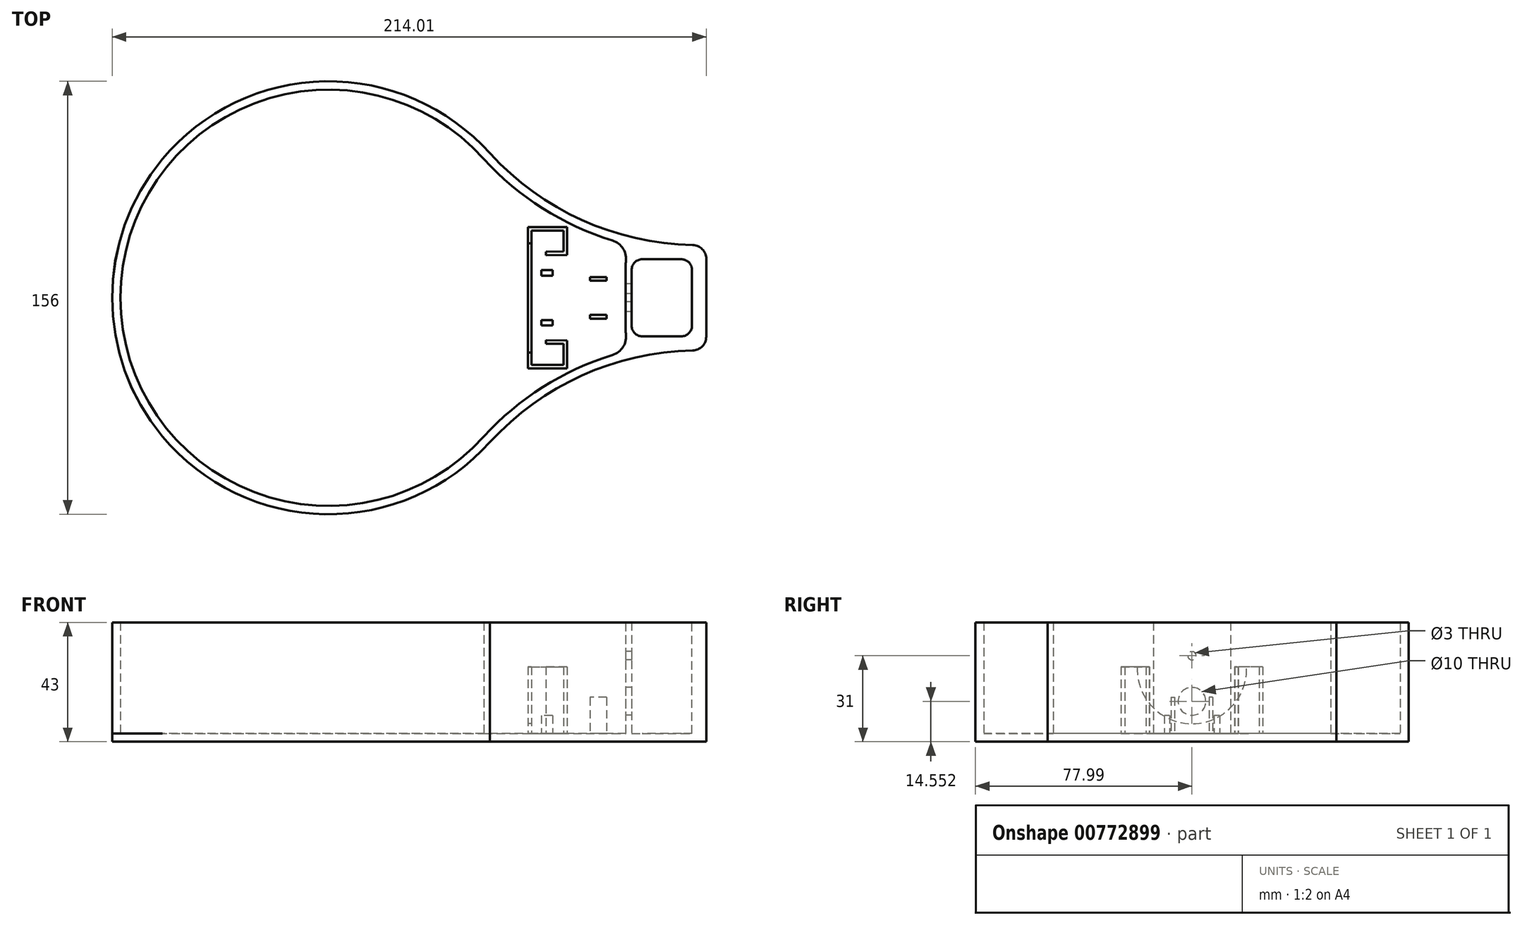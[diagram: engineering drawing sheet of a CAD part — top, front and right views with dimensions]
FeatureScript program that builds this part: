
annotation { "Feature Type Name" : "Feature", "Feature Type Description" : "" }
export const myFeature = defineFeature(function(context is Context, id is Id, definition is map)
    precondition{}
    {
        {
            var Q0;
            Q0=qCreatedBy(makeId("Top.planeOp"),FACE);
            var sketch = newSketch(context, id + "F0", { "sketchPlane" : qUnion([Q0])});
            skLineSegment(sketch, "E0", {"start": v(133, 0) * mm, "end": v(133, 16) * mm});
            skLineSegment(sketch, "E1", {"start": v(133, 16) * mm, "end": v(132.98, -16) * mm});
            skLineSegment(sketch, "E2", {"start": v(132.98, -16) * mm, "end": v(106.98, -16) * mm});
            skLineSegment(sketch, "E3", {"start": v(106.98, -16) * mm, "end": v(106.98, 16) * mm});
            skLineSegment(sketch, "E4", {"start": v(106.98, 16) * mm, "end": v(133, 16) * mm});
            skArc(sketch, "E5", {"start": v(55.9, 50) * mm, "mid": v(90.87, 24.88) * mm, "end": v(133, 16) * mm});
            skArc(sketch, "E6", {"start": v(132.98, -16) * mm, "mid": v(90.85, -24.88) * mm, "end": v(55.88, -50) * mm});
            skLineSegment(sketch, "E7", {"start": v(85.88, 25.5) * mm, "end": v(71.8, 25.5) * mm});
            skLineSegment(sketch, "E8", {"start": v(71.8, 25.5) * mm, "end": v(71.8, -25.5) * mm});
            skLineSegment(sketch, "E9", {"start": v(71.8, -25.5) * mm, "end": v(85.88, -25.5) * mm});
            skArc(sketch, "E10", {"start": v(55.9, 50) * mm, "mid": v(-75.01, 0.02) * mm, "end": v(55.88, -50) * mm});
            skLineSegment(sketch, "E11.0", {"start": v(109.1, 13.88) * mm, "end": v(130.88, 13.88) * mm});
            skLineSegment(sketch, "E11.1", {"start": v(109.1, -13.88) * mm, "end": v(109.1, 13.88) * mm});
            skLineSegment(sketch, "E11.2", {"start": v(130.86, -13.88) * mm, "end": v(109.1, -13.88) * mm});
            skLineSegment(sketch, "E11.3", {"start": v(130.88, 13.88) * mm, "end": v(130.86, -13.88) * mm});
            skLineSegment(sketch, "E12.0", {"start": v(84.6, 24.2) * mm, "end": v(73.1, 24.2) * mm});
            skLineSegment(sketch, "E12.2", {"start": v(73.1, -24.2) * mm, "end": v(84.6, -24.2) * mm});
            skLineSegment(sketch, "E12.3", {"start": v(73.1, 24.2) * mm, "end": v(73.1, -24.2) * mm});
            skLineSegment(sketch, "E13", {"start": v(85.88, 25.5) * mm, "end": v(85.88, 15.4) * mm});
            skLineSegment(sketch, "E14", {"start": v(85.88, 15.4) * mm, "end": v(78.28, 15.3) * mm});
            skLineSegment(sketch, "E15", {"start": v(78.28, 15.3) * mm, "end": v(78.27, 16.6) * mm});
            skLineSegment(sketch, "E16", {"start": v(78.27, 16.6) * mm, "end": v(84.6, 16.68) * mm});
            skLineSegment(sketch, "E17", {"start": v(85.88, -25.5) * mm, "end": v(85.88, -15.4) * mm});
            skLineSegment(sketch, "E18", {"start": v(85.88, -15.4) * mm, "end": v(78.28, -15.3) * mm});
            skLineSegment(sketch, "E19", {"start": v(78.28, -15.3) * mm, "end": v(78.28, -16.6) * mm});
            skLineSegment(sketch, "E20", {"start": v(78.28, -16.6) * mm, "end": v(84.6, -16.6) * mm});
            skLineSegment(sketch, "E21", {"start": v(84.6, -16.6) * mm, "end": v(84.6, -24.2) * mm});
            skLineSegment(sketch, "E22", {"start": v(84.6, 24.2) * mm, "end": v(84.6, 16.68) * mm});
            skArc(sketch, "E23.0", {"start": v(58.13, 52.01) * mm, "mid": v(93.46, 27.02) * mm, "end": v(136, 19.04) * mm});
            skArc(sketch, "E23.1", {"start": v(58.13, 52.01) * mm, "mid": v(-78.01, 0.02) * mm, "end": v(58.1, -52.01) * mm});
            skArc(sketch, "E23.2", {"start": v(135.98, -19.04) * mm, "mid": v(93.44, -27.02) * mm, "end": v(58.1, -52.01) * mm});
            skLineSegment(sketch, "E23.3", {"start": v(136, 19.04) * mm, "end": v(135.98, -19.04) * mm});
            skArc(sketch, "E24", {"start": v(-59.9, 50) * mm, "mid": v(-77.99, 0) * mm, "end": v(-59.87, -50) * mm});
            skSolve(sketch);
        }
        {
            var Q0;
            Q0=makeQuery(id+"F0.imprint","IMPRINT",FACE,{"disambiguationData":[TD([[makeQuery(id+"F0.imprint","IMPRINT",EDGE,{"derivedFrom":sQuery(id+"F0.wireOp",EDGE,"E1")}),1.0]])]});
            extrude(context, id + "F1", {"entities" : qUnion([Q0]), "depth" : 40 * mm, "offsetDistance" : 25 * mm});
        }
        {
            var Q0;
            Q0 = qSketchRegion(id + "F0", true);
            var Q1;
            Q1=makeQuery(id+"F0.imprint","IMPRINT",FACE,{"disambiguationData":[TD([[makeQuery(id+"F0.imprint","IMPRINT",EDGE,{"derivedFrom":sQuery(id+"F0.wireOp",EDGE,"E2")}),1.0]])]});
            var Q2;
            Q2=makeQuery(id+"F0.imprint","IMPRINT",FACE,{"disambiguationData":[TD([[makeQuery(id+"F0.imprint","IMPRINT",EDGE,{"derivedFrom":sQuery(id+"F0.wireOp",EDGE,"E1")}),-1.0]])]});
            var Q3;
            Q3=makeQuery(id+"F0.imprint","IMPRINT",FACE,{"disambiguationData":[TD([[makeQuery(id+"F0.imprint","IMPRINT",EDGE,{"derivedFrom":sQuery(id+"F0.wireOp",EDGE,"E11.0")}),-1.0]])]});
            var Q4;
            Q4=makeQuery(id+"F0.imprint","IMPRINT",FACE,{"disambiguationData":[TD([[makeQuery(id+"F0.imprint","IMPRINT",EDGE,{"derivedFrom":sQuery(id+"F0.wireOp",EDGE,"E7")}),1.0]])]});
            extrude(context, id + "F2", {"entities" : qUnion([Q0, Q1, Q2, Q3, Q4]), "operationType" : NewBodyOperationType.ADD, "oppositeDirection" : true, "depth" : 3 * mm, "offsetDistance" : 25 * mm});
        }
        {
            var Q0;
            Q0=makeQuery(id+"F0.imprint","IMPRINT",FACE,{"disambiguationData":[TD([[makeQuery(id+"F0.imprint","IMPRINT",EDGE,{"derivedFrom":sQuery(id+"F0.wireOp",EDGE,"E7")}),1.0]])]});
            extrude(context, id + "F3", {"entities" : qUnion([Q0]), "operationType" : NewBodyOperationType.ADD, "depth" : 24 * mm, "offsetDistance" : 25 * mm});
        }
        {
            var Q0;
            Q0=makeQuery(id+"F0.imprint","IMPRINT",FACE,{"disambiguationData":[TD([[makeQuery(id+"F0.imprint","IMPRINT",EDGE,{"derivedFrom":sQuery(id+"F0.wireOp",EDGE,"E1")}),-1.0]])]});
            extrude(context, id + "F4", {"entities" : qUnion([Q0]), "operationType" : NewBodyOperationType.ADD, "depth" : 40 * mm, "offsetDistance" : 25 * mm});
        }
        {
            var Q0;
            Q0=makeQuery(id+"F3.opExtrude","SWEPT_FACE",FACE,{"disambiguationData":[OSD([sQuery(id+"F0.wireOp",EDGE,"E8")])]});
            var sketch = newSketch(context, id + "F5", { "sketchPlane" : qUnion([Q0])});
            skArc(sketch, "E25", {"start": v(-19.7, 24) * mm, "mid": v(0, 3.5) * mm, "end": v(19.7, 24) * mm});
            skSolve(sketch);
        }
        {
            var Q0;
            {var subQ0=sQuery(id+"F5.wireOp",EDGE,"E25");Q0=makeQuery(id+"F5.imprint","IMPRINT",FACE,{"disambiguationData":[TD([[makeQuery(id+"F5.imprint","IMPRINT",EDGE,{"derivedFrom":subQ0}),1.0]])]});}
            extrude(context, id + "F6", {"entities" : qUnion([Q0]), "operationType" : NewBodyOperationType.REMOVE, "oppositeDirection" : true, "depth" : 2.5 * mm, "offsetDistance" : 25 * mm});
        }
        {
            var Q0;
            Q0=makeQuery(id+"F0.imprint","IMPRINT",FACE,{"disambiguationData":[TD([[makeQuery(id+"F0.imprint","IMPRINT",EDGE,{"derivedFrom":sQuery(id+"F0.wireOp",EDGE,"E2")}),1.0]])]});
            var sketch = newSketch(context, id + "F7", { "sketchPlane" : qUnion([Q0])});
            skLineSegment(sketch, "E26.bottom", {"start": v(100.13, 7.46) * mm, "end": v(94.13, 7.46) * mm});
            skLineSegment(sketch, "E26.top", {"start": v(100.13, 6.16) * mm, "end": v(94.13, 6.16) * mm});
            skLineSegment(sketch, "E26.left", {"start": v(100.13, 7.46) * mm, "end": v(100.13, 6.16) * mm});
            skLineSegment(sketch, "E26.right", {"start": v(94.13, 7.46) * mm, "end": v(94.13, 6.16) * mm});
            skLineSegment(sketch, "E27.bottom", {"start": v(100.13, -7.5) * mm, "end": v(94.13, -7.5) * mm});
            skLineSegment(sketch, "E27.top", {"start": v(100.13, -6.2) * mm, "end": v(94.13, -6.2) * mm});
            skLineSegment(sketch, "E27.left", {"start": v(100.13, -7.5) * mm, "end": v(100.13, -6.2) * mm});
            skLineSegment(sketch, "E27.right", {"start": v(94.13, -7.5) * mm, "end": v(94.13, -6.2) * mm});
            skSolve(sketch);
        }
        {
            var Q0;
            Q0=makeQuery(id+"F7.imprint","IMPRINT",FACE,{"disambiguationData":[TD([[makeQuery(id+"F7.imprint","IMPRINT",EDGE,{"derivedFrom":sQuery(id+"F7.wireOp",EDGE,"E26.bottom")}),1.0]])]});
            var Q1;
            Q1=makeQuery(id+"F7.imprint","IMPRINT",FACE,{"disambiguationData":[TD([[makeQuery(id+"F7.imprint","IMPRINT",EDGE,{"derivedFrom":sQuery(id+"F7.wireOp",EDGE,"E27.bottom")}),-1.0]])]});
            extrude(context, id + "F8", {"entities" : qUnion([Q0, Q1]), "operationType" : NewBodyOperationType.ADD, "depth" : 13 * mm, "offsetDistance" : 25 * mm});
        }
        {
            var Q0;
            Q0=makeQuery(id+"F0.imprint","IMPRINT",FACE,{"disambiguationData":[TD([[makeQuery(id+"F0.imprint","IMPRINT",EDGE,{"derivedFrom":sQuery(id+"F0.wireOp",EDGE,"E2")}),1.0]])]});
            var sketch = newSketch(context, id + "F9", { "sketchPlane" : qUnion([Q0])});
            skLineSegment(sketch, "E28", {"start": v(80.62, 10) * mm, "end": v(76.62, 10) * mm});
            skLineSegment(sketch, "E29", {"start": v(76.62, 10) * mm, "end": v(76.62, 8) * mm});
            skLineSegment(sketch, "E30", {"start": v(76.62, 8) * mm, "end": v(80.62, 8) * mm});
            skLineSegment(sketch, "E31", {"start": v(80.62, -10) * mm, "end": v(76.62, -10) * mm});
            skLineSegment(sketch, "E32", {"start": v(76.62, -10) * mm, "end": v(76.62, -8) * mm});
            skLineSegment(sketch, "E33", {"start": v(76.62, -8) * mm, "end": v(80.62, -8) * mm});
            skLineSegment(sketch, "E34", {"start": v(80.62, 10) * mm, "end": v(80.62, 8) * mm});
            skLineSegment(sketch, "E35", {"start": v(80.62, -8) * mm, "end": v(80.62, -10) * mm});
            skSolve(sketch);
        }
        {
            var Q0;
            Q0=makeQuery(id+"F9.imprint","IMPRINT",FACE,{"disambiguationData":[TD([[makeQuery(id+"F9.imprint","IMPRINT",EDGE,{"derivedFrom":sQuery(id+"F9.wireOp",EDGE,"E28")}),1.0]])]});
            var Q1;
            Q1=makeQuery(id+"F9.imprint","IMPRINT",FACE,{"disambiguationData":[TD([[makeQuery(id+"F9.imprint","IMPRINT",EDGE,{"derivedFrom":sQuery(id+"F9.wireOp",EDGE,"E31")}),-1.0]])]});
            extrude(context, id + "F10", {"entities" : qUnion([Q0, Q1]), "operationType" : NewBodyOperationType.ADD, "depth" : 6.5 * mm, "offsetDistance" : 25 * mm});
        }
        {
            var Q0;
            Q0=makeQuery(id+"F4.opExtrude","SWEPT_FACE",FACE,{"disambiguationData":[OSD([sQuery(id+"F0.wireOp",EDGE,"E3")])]});
            var sketch = newSketch(context, id + "F11", { "sketchPlane" : qUnion([Q0])});
            skCircle(sketch, "E36", {"center": v(0, 28) * mm, "radius": 1.5 * mm});
            skSolve(sketch);
        }
        {
            var Q0;
            Q0=makeQuery(id+"F11.imprint","IMPRINT",FACE,{"disambiguationData":[TD([[makeQuery(id+"F11.imprint","IMPRINT",EDGE,{"derivedFrom":sQuery(id+"F11.wireOp",EDGE,"E36")}),1.0]])]});
            extrude(context, id + "F12", {"entities" : qUnion([Q0]), "operationType" : NewBodyOperationType.REMOVE, "oppositeDirection" : true, "depth" : 3.5 * mm, "offsetDistance" : 25 * mm});
        }
        {
            var Q0;
            Q0=makeQuery(id+"F4.opExtrude","SWEPT_FACE",FACE,{"disambiguationData":[OSD([sQuery(id+"F0.wireOp",EDGE,"E3")])]});
            var sketch = newSketch(context, id + "F13", { "sketchPlane" : qUnion([Q0])});
            skCircle(sketch, "E37", {"center": v(0, 11.55) * mm, "radius": 5 * mm});
            skSolve(sketch);
        }
        {
            var Q0;
            Q0=makeQuery(id+"F13.imprint","IMPRINT",FACE,{"disambiguationData":[TD([[makeQuery(id+"F13.imprint","IMPRINT",EDGE,{"derivedFrom":sQuery(id+"F13.wireOp",EDGE,"E37")}),1.0]])]});
            extrude(context, id + "F14", {"entities" : qUnion([Q0]), "operationType" : NewBodyOperationType.REMOVE, "oppositeDirection" : true, "depth" : 2.5 * mm, "offsetDistance" : 25 * mm});
        }
        {
            var Q0;
            Q0=makeQuery(id+"F4.opExtrude","SWEPT_EDGE",EDGE,{"disambiguationData":[OSD([sQuery(id+"F0.wireOp",EDGE,"E11.0"),sQuery(id+"F0.wireOp",EDGE,"E11.3")])]});
            var Q1;
            Q1=makeQuery(id+"F4.opExtrude","SWEPT_EDGE",EDGE,{"disambiguationData":[OSD([sQuery(id+"F0.wireOp",EDGE,"E3"),sQuery(id+"F0.wireOp",EDGE,"E4")])]});
            var Q2;
            Q2=makeQuery(id+"F4.opExtrude","SWEPT_EDGE",EDGE,{"disambiguationData":[OSD([sQuery(id+"F0.wireOp",EDGE,"E11.0"),sQuery(id+"F0.wireOp",EDGE,"E11.1")])]});
            var Q3;
            Q3=makeQuery(id+"F4.opExtrude","SWEPT_EDGE",EDGE,{"disambiguationData":[OSD([sQuery(id+"F0.wireOp",EDGE,"E11.2"),sQuery(id+"F0.wireOp",EDGE,"E11.3")])]});
            var Q4;
            Q4=makeQuery(id+"F4.opExtrude","SWEPT_EDGE",EDGE,{"disambiguationData":[OSD([sQuery(id+"F0.wireOp",EDGE,"E2"),sQuery(id+"F0.wireOp",EDGE,"E3")])]});
            var Q5;
            Q5=makeQuery(id+"F4.opExtrude","SWEPT_EDGE",EDGE,{"disambiguationData":[OSD([sQuery(id+"F0.wireOp",EDGE,"E11.1"),sQuery(id+"F0.wireOp",EDGE,"E11.2")])]});
            fillet(context, id + "F15", {"entities" : qUnion([Q0, Q1, Q2, Q3, Q4, Q5]), "radius" : 3.86 * mm, "tangentPropagation" : true, "allowEdgeOverflow" : false});
        }
        {
            var Q0;
            {var subQ0=sQuery(id+"F0.wireOp",EDGE,"E6");var subQ1=sQuery(id+"F0.wireOp",EDGE,"E2");var subQ2=sQuery(id+"F0.wireOp",EDGE,"E1");Q0=makeQuery(id+"F4.boolean.opBoolean","MERGE",EDGE,{"derivedFrom":[makeQuery(id+"F1.opExtrude","SWEPT_EDGE",EDGE,{"disambiguationData":[OSD([subQ2,subQ1,subQ0])]}),makeQuery(id+"F4.opExtrude","SWEPT_EDGE",EDGE,{"disambiguationData":[OSD([subQ2,subQ1,subQ0])]})]});}
            fillet(context, id + "F16", {"entities" : qUnion([Q0]), "radius" : 7 * mm, "tangentPropagation" : true, "allowEdgeOverflow" : false});
        }
        {
            var Q0;
            {var subQ0=sQuery(id+"F0.wireOp",EDGE,"E5");var subQ1=sQuery(id+"F0.wireOp",EDGE,"E4");var subQ2=sQuery(id+"F0.wireOp",EDGE,"E1");Q0=makeQuery(id+"F4.boolean.opBoolean","MERGE",EDGE,{"derivedFrom":[makeQuery(id+"F1.opExtrude","SWEPT_EDGE",EDGE,{"disambiguationData":[OSD([subQ2,subQ1,subQ0])]}),makeQuery(id+"F4.opExtrude","SWEPT_EDGE",EDGE,{"disambiguationData":[OSD([subQ2,subQ1,subQ0])]})]});}
            fillet(context, id + "F17", {"entities" : qUnion([Q0]), "radius" : 7 * mm, "tangentPropagation" : true, "allowEdgeOverflow" : false});
        }
        {
            var Q0;
            {var subQ0=sQuery(id+"F0.wireOp",EDGE,"E23.3");var subQ1=sQuery(id+"F0.wireOp",EDGE,"E23.2");Q0=makeQuery(id+"F2.boolean.opBoolean","MERGE",EDGE,{"derivedFrom":[makeQuery(id+"F1.opExtrude","SWEPT_EDGE",EDGE,{"disambiguationData":[OSD([subQ1,subQ0])]}),makeQuery(id+"F2.opExtrude","SWEPT_EDGE",EDGE,{"disambiguationData":[OSD([subQ1,subQ0])]})]});}
            var Q1;
            {var subQ0=sQuery(id+"F0.wireOp",EDGE,"E23.3");var subQ1=sQuery(id+"F0.wireOp",EDGE,"E23.0");Q1=makeQuery(id+"F2.boolean.opBoolean","MERGE",EDGE,{"derivedFrom":[makeQuery(id+"F1.opExtrude","SWEPT_EDGE",EDGE,{"disambiguationData":[OSD([subQ1,subQ0])]}),makeQuery(id+"F2.opExtrude","SWEPT_EDGE",EDGE,{"disambiguationData":[OSD([subQ1,subQ0])]})]});}
            fillet(context, id + "F18", {"entities" : qUnion([Q0, Q1]), "radius" : 5 * mm, "tangentPropagation" : true, "allowEdgeOverflow" : false});
        }
    });
